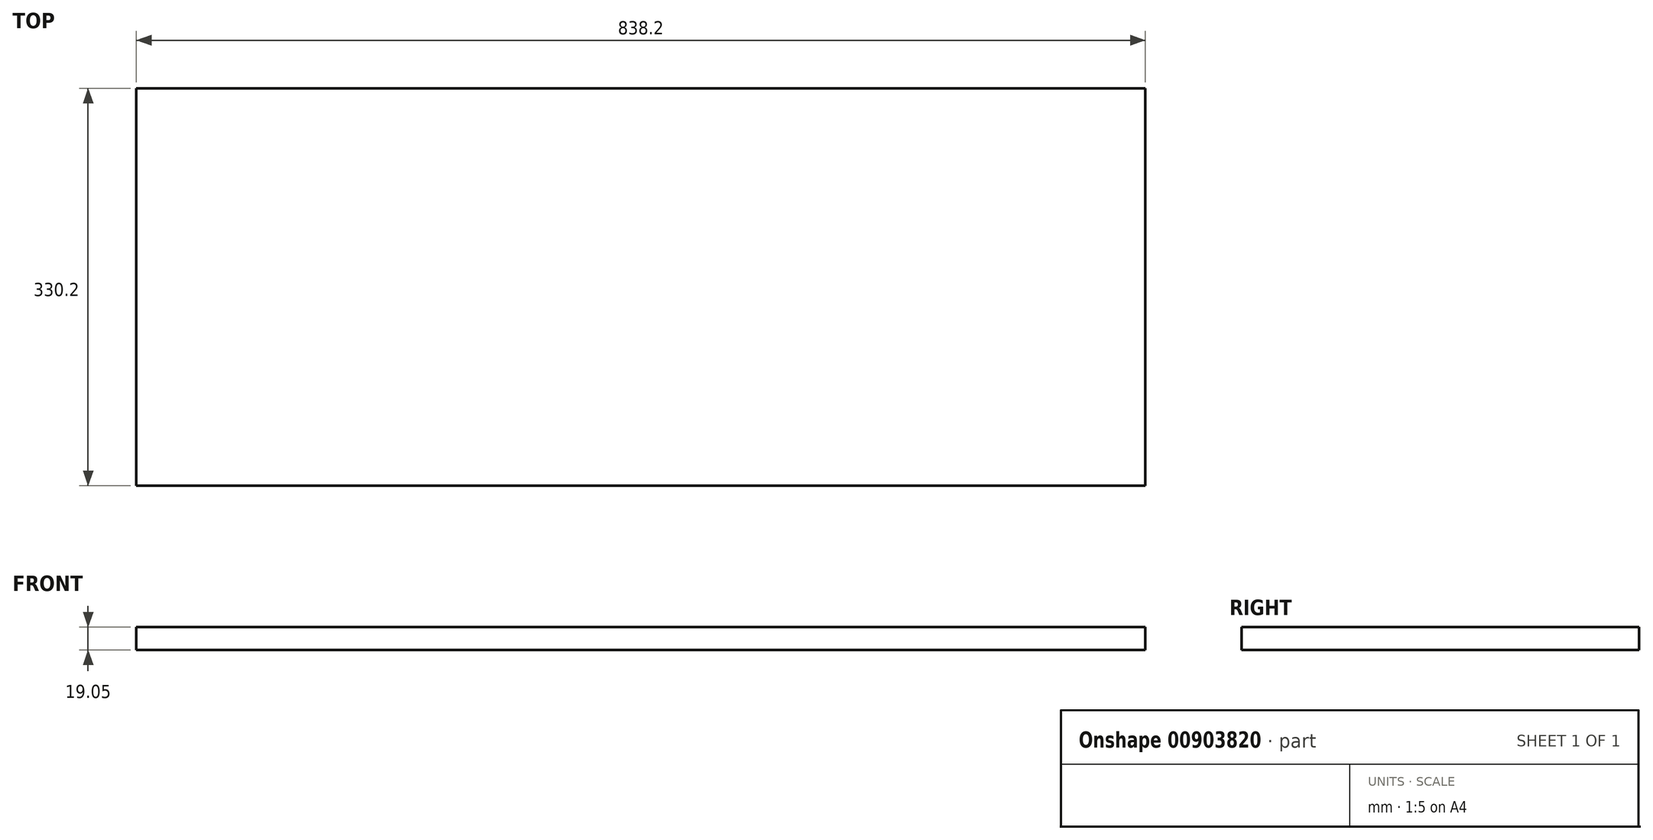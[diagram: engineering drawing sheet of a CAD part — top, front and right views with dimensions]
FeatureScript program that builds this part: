
annotation { "Feature Type Name" : "Feature", "Feature Type Description" : "" }
export const myFeature = defineFeature(function(context is Context, id is Id, definition is map)
    precondition{}
    {
        {
            var Q0;
            Q0=qCreatedBy(makeId("Top.planeOp"),FACE);
            var sketch = newSketch(context, id + "F0", { "sketchPlane" : qUnion([Q0])});
            skLineSegment(sketch, "E0.bottom", {"start": v(0, 0) * mm, "end": v(838.2, 0) * mm});
            skLineSegment(sketch, "E0.top", {"start": v(0, 330.2) * mm, "end": v(838.2, 330.2) * mm});
            skLineSegment(sketch, "E0.left", {"start": v(0, 0) * mm, "end": v(0, 330.2) * mm});
            skLineSegment(sketch, "E0.right", {"start": v(838.2, 0) * mm, "end": v(838.2, 330.2) * mm});
            skSolve(sketch);
        }
        {
            var Q0;
            Q0 = qSketchRegion(id + "F0", true);
            extrude(context, id + "F1", {"entities" : qUnion([Q0]), "depth" : 19.05 * mm, "offsetDistance" : 25.4 * mm});
        }
    });
